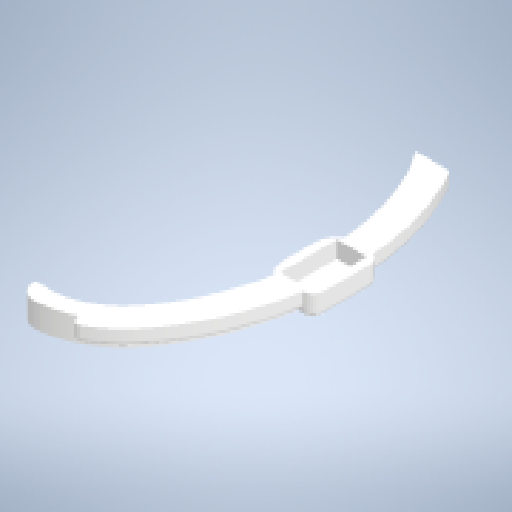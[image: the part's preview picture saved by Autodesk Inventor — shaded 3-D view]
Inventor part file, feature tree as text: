
AUTODESK INVENTOR PART (.ipt)
format: ipt  version: 2025.2 (Build 292293000, 293)  size: 528,384 bytes
history: native  units: in
note: dims shown in document units (in); Inventor stores cm internally (conversion verified against a paired STEP export)
features: fillet x6, extrude x5, sketch x5, other x3, reference x1
ambient origin geometry x8: Origin, YZ Plane, XZ Plane, XY Plane, X Axis, Y Axis, Z Axis, Center Point
bodies: Solid1 (feature_tree), Body1 (feature_tree)
feature tree (20):
  extrude  "Extrusion3"  Depth=0.1693in
  extrude  "Extrusion4"  Depth=0.0787in TaperAngle=0.0deg
  fillet  "Fillet13"  Radius=0.1063in
  fillet  "Fillet14"  Radius=0.2047in
  fillet  "Fillet15"  Radius=0.0591in
  fillet  "Fillet16"  Radius=0.0394in
  fillet  "Fillet17"  Radius=0.0394in
  fillet  "Fillet18"  Radius=0.0213in
  extrude  "Extrusion5"  Depth=0.0787in
  extrude  "Extrusion6"  Depth=0.7992in TaperAngle=0.0deg
  extrude  "Extrusion7"  Depth=0.1117in TaperAngle=0.0deg
  sketch  "Sketch3"  dims[d29=90.0deg d30=0.1693in]
  reference  "Reference1"
  sketch  "Sketch4"  dims[d31=0.2441in d32=0.0787in d33=0.0in d34=0.1063in d35=0.2047in d36=0.0591in d37=0.0in d38=0.0394in d39=0.0394in d40=0.0213in]
  sketch  "Sketch5"  dims[d41=0.0787in d42=0.0787in]
  sketch  "Sketch6"  dims[d43=0.0197in d44=0.7992in d45=0.0in]
  sketch  "Sketch7"  dims[d46=0.1117in d47=0.0in d48=0.1117in d49=0.0in d18=0.0in d19=0.0in d20=0.0in d21=0.0in d22=0.0in d23=0.0in]
  other  "<userpath>\Downloads\rat_cap_EC_v12 v0\rat_cap_walls_v8.iam"
  other  "rat_cap_walls_v8.iam"
  other  "rat_cap_left_wall_v8:1"
